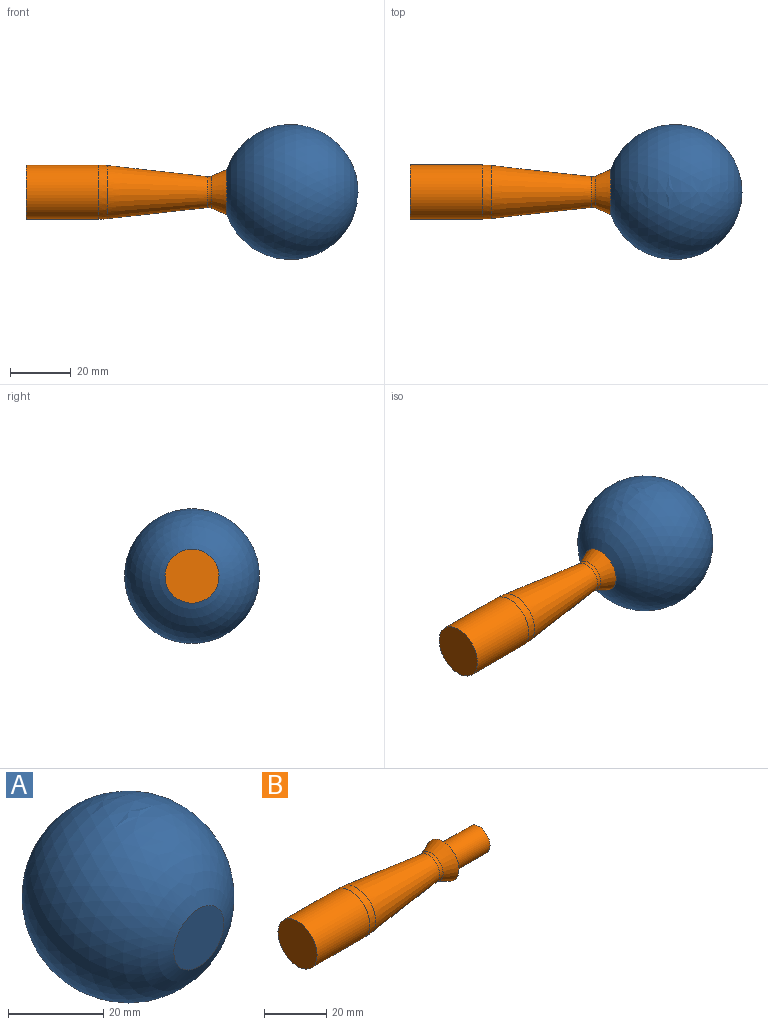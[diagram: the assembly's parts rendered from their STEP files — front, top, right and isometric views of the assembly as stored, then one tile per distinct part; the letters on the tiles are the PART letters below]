
ASSEMBLY  parts=2 mates=1
PART A: 2 faces, bbox 44.5x43.2x44.5 mm
  f0: sphere r=22.23mm, area 6029.8mm2, adj f1
  f1: plane 14.81x14.81mm, normal (0,-1,0), area 172.3mm2, adj f0
PART B: 9 faces, bbox 82.6x17.8x17.8 mm
  f0: plane 10.01x10.01mm, normal (1,0,0), area 78.7mm2, adj f1
  f1: cylinder r=5mm len=16.51mm, axis (1,0,0), area 519.1mm2, adj f0,f2
  f2: plane 14.83x14.83mm, normal (1,0,0), area 94.2mm2, adj f1,f3
  f3: cone r=7.42mm half-angle=22.9deg, axis (1,0,0), area 220.7mm2, adj f2,f4
  f4: torus R=7.6mm, axis (1,0,0), area 41.7mm2, adj f3,f5
  f5: cone r=5.08mm half-angle=6.3deg, axis (-1,0,0), area 1434.9mm2, adj f4,f6
  f6: revolved ~17.78x17.78mm, area 156.3mm2, adj f5,f7
  f7: cylinder r=8.89mm len=23.99mm, axis (1,0,0), area 1340.1mm2, adj f6,f8
  f8: plane 17.78x17.78mm, normal (-1,0,0), area 248.3mm2, adj f7
PLACE A rot(axis=(0,0,-1),90deg) t=(3.35,0,1.94)mm
PLACE B t=(-23.32,0,1.94)mm
MATE planar A.f1 <-> B.f3  axis (-1,0,0) through (-39.83,0,1.94)mm
